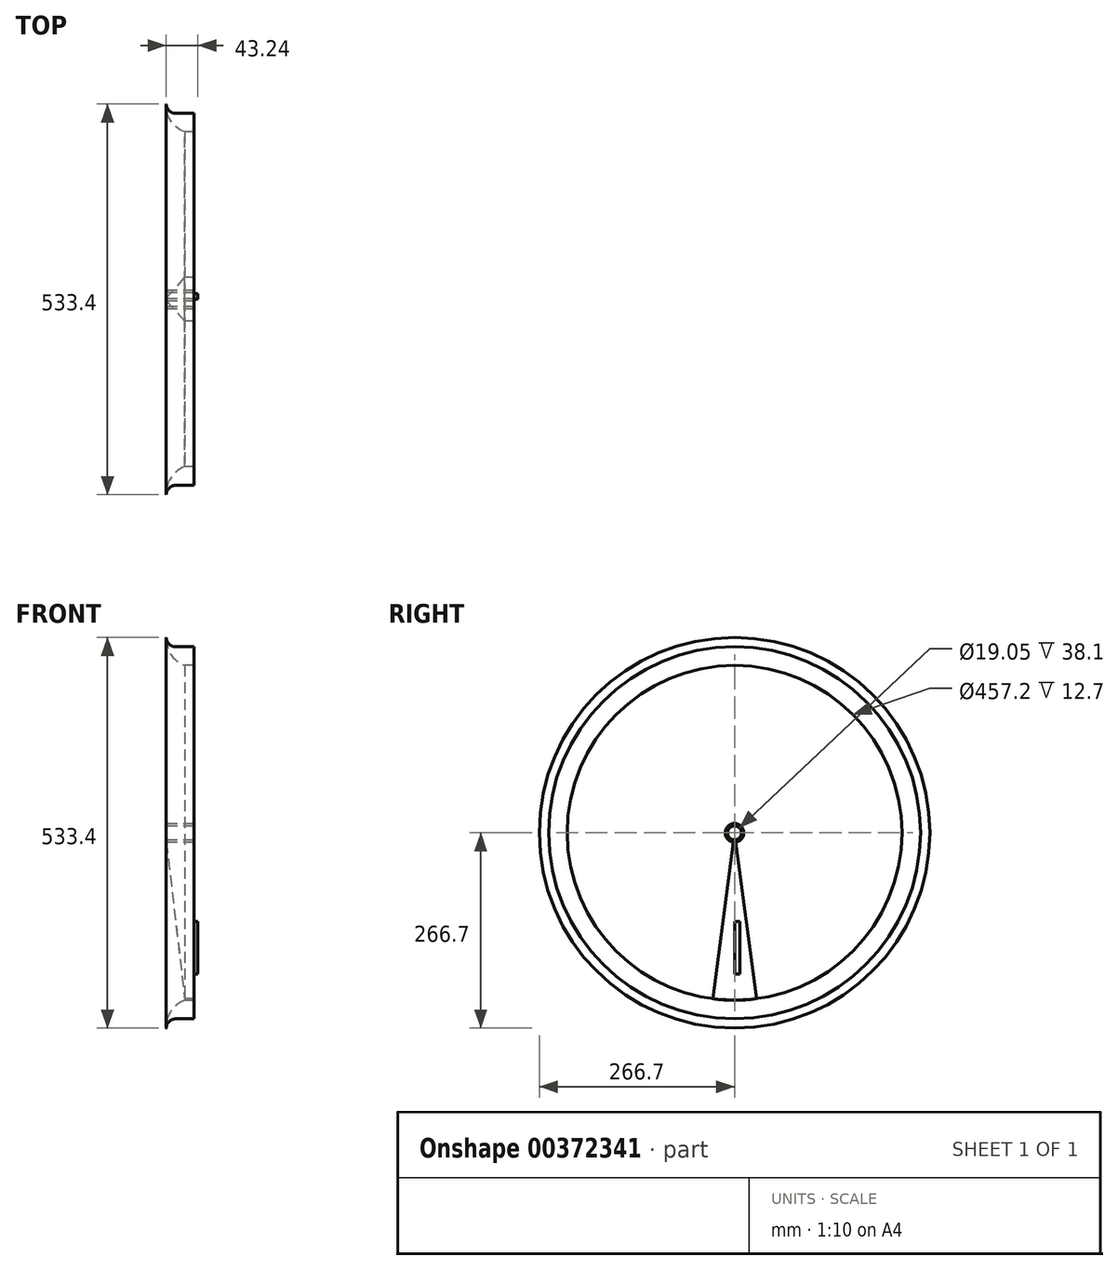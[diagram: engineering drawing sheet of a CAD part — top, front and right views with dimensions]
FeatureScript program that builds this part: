
annotation { "Feature Type Name" : "Feature", "Feature Type Description" : "" }
export const myFeature = defineFeature(function(context is Context, id is Id, definition is map)
    precondition{}
    {
        {
            var Q0;
            Q0=qCreatedBy(makeId("Front.planeOp"),FACE);
            var sketch = newSketch(context, id + "F0", { "sketchPlane" : qUnion([Q0])});
            skLineSegment(sketch, "E0", {"start": v(-81.53, 0) * mm, "end": v(81.04, 0) * mm});
            skLineSegment(sketch, "E1", {"start": v(0, 254) * mm, "end": v(-25.4, 254) * mm});
            skLineSegment(sketch, "E2", {"start": v(0, 254) * mm, "end": v(0, 228.6) * mm});
            skLineSegment(sketch, "E3", {"start": v(0, 228.6) * mm, "end": v(-12.7, 228.6) * mm});
            skArc(sketch, "E4", {"start": v(-38.1, 266.7) * mm, "mid": v(-34.38, 257.72) * mm, "end": v(-25.4, 254) * mm});
            skArc(sketch, "E5", {"start": v(-38.1, 266.7) * mm, "mid": v(-31.74, 243.42) * mm, "end": v(-12.7, 228.6) * mm});
            skSolve(sketch);
        }
        {
            var Q0;
            Q0=qCreatedBy(makeId("Right.planeOp"),FACE);
            var sketch = newSketch(context, id + "F1", { "sketchPlane" : qUnion([Q0])});
            skCircle(sketch, "E6", {"center": v(0, 0) * mm, "radius": 9.53 * mm});
            skCircle(sketch, "E7", {"center": v(0, 0) * mm, "radius": 12.7 * mm});
            skSolve(sketch);
        }
        {
            var Q0;
            Q0=makeQuery(id+"F1.imprint","IMPRINT",FACE,{"disambiguationData":[TD([[makeQuery(id+"F1.imprint","IMPRINT",EDGE,{"derivedFrom":sQuery(id+"F1.wireOp",EDGE,"E6")}),-1.0]])]});
            extrude(context, id + "F2", {"entities" : qUnion([Q0]), "oppositeDirection" : true, "depth" : 38.1 * mm});
        }
        {
            var Q0;
            Q0=makeQuery(id+"F0.imprint","IMPRINT",FACE,{"disambiguationData":[TD([[makeQuery(id+"F0.imprint","IMPRINT",EDGE,{"derivedFrom":sQuery(id+"F0.wireOp",EDGE,"E1")}),1.0]])]});
            var Q1;
            Q1=sQuery(id+"F0.wireOp",EDGE,"E0");
            revolve(context, id + "F3", {"entities" : qUnion([Q0]), "axis" : qUnion([Q1]), "revolveType" : RevolveType.FULL});
        }
        {
            var Q0;
            Q0=qCreatedBy(makeId("Front.planeOp"),FACE);
            var sketch = newSketch(context, id + "F4", { "sketchPlane" : qUnion([Q0])});
            skLineSegment(sketch, "E8", {"start": v(0, -12.7) * mm, "end": v(0, -228.6) * mm});
            skLineSegment(sketch, "E9", {"start": v(0, -228.6) * mm, "end": v(-12.7, -228.6) * mm});
            skLineSegment(sketch, "E10", {"start": v(-38.1, -12.7) * mm, "end": v(-12.7, -228.6) * mm});
            skLineSegment(sketch, "E11", {"start": v(-38.1, -12.7) * mm, "end": v(0, -12.7) * mm});
            skLineSegment(sketch, "E12", {"start": v(0, 0) * mm, "end": v(-57.33, 0) * mm});
            skSolve(sketch);
        }
        {
            var Q0;
            Q0=makeQuery(id+"F4.imprint","IMPRINT",FACE,{"disambiguationData":[TD([[makeQuery(id+"F4.imprint","IMPRINT",EDGE,{"derivedFrom":sQuery(id+"F4.wireOp",EDGE,"E8")}),-1.0]])]});
            var Q1;
            Q1=sQuery(id+"F4.wireOp",EDGE,"E12");
            revolve(context, id + "F5", {"entities" : qUnion([Q0]), "axis" : qUnion([Q1]), "revolveType" : RevolveType.SYMMETRIC, "angle" : 15 * degree});
        }
        {
            var Q0;
            Q0=qCreatedBy(makeId("Front.planeOp"),FACE);
            var sketch = newSketch(context, id + "F6", { "sketchPlane" : qUnion([Q0])});
            skLineSegment(sketch, "E13", {"start": v(0, 0) * mm, "end": v(-95.14, 0) * mm});
            skSolve(sketch);
        }
        {
            var Q0;
            Q0=qCreatedBy(makeId("Right.planeOp"),FACE);
            var sketch = newSketch(context, id + "F7", { "sketchPlane" : qUnion([Q0])});
            skLineSegment(sketch, "E14.bottom", {"start": v(0, -192.7) * mm, "end": v(7.5, -192.7) * mm});
            skLineSegment(sketch, "E14.top", {"start": v(0, -121.24) * mm, "end": v(7.5, -121.24) * mm});
            skLineSegment(sketch, "E14.left", {"start": v(0, -192.7) * mm, "end": v(0, -121.24) * mm});
            skLineSegment(sketch, "E14.right", {"start": v(7.5, -192.7) * mm, "end": v(7.5, -121.24) * mm});
            skSolve(sketch);
        }
        {
            var Q0;
            Q0=makeQuery(id+"F7.imprint","IMPRINT",FACE,{"disambiguationData":[TD([[makeQuery(id+"F7.imprint","IMPRINT",EDGE,{"derivedFrom":sQuery(id+"F7.wireOp",EDGE,"E14.bottom")}),1.0]])]});
            extrude(context, id + "F8", {"entities" : qUnion([Q0]), "operationType" : NewBodyOperationType.ADD, "depth" : 5.08 * mm});
        }
    });
